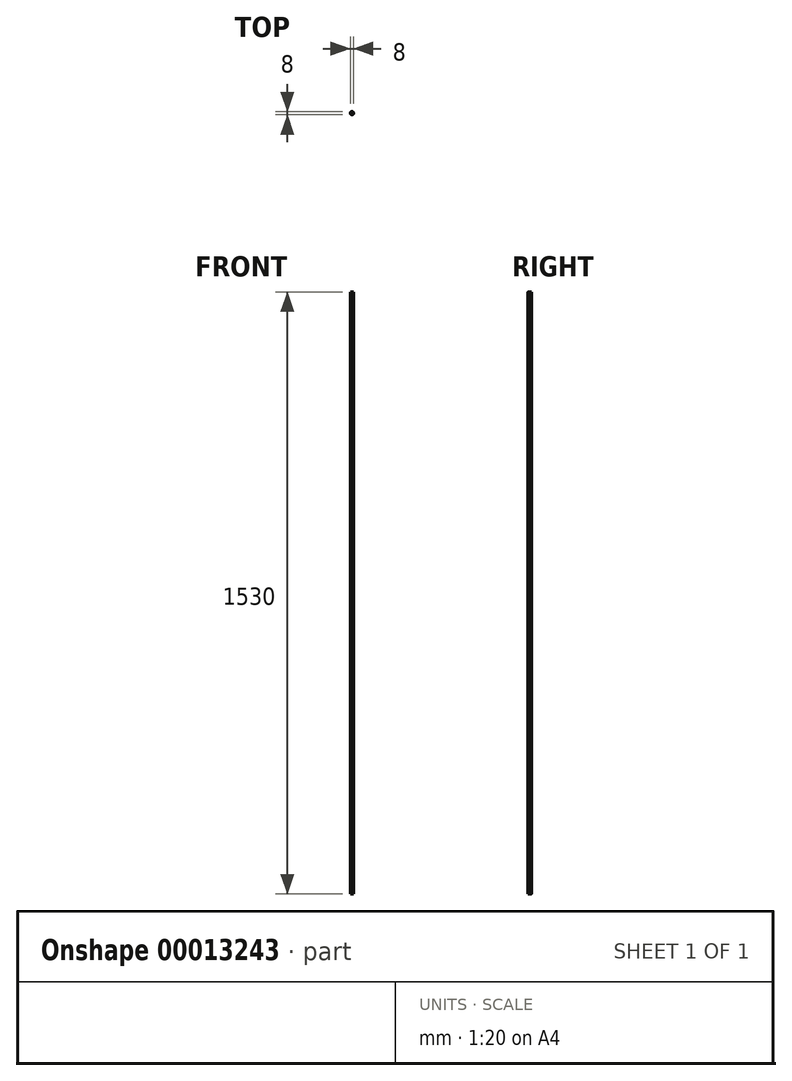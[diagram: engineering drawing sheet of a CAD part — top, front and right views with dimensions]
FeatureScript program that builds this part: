
annotation { "Feature Type Name" : "Feature", "Feature Type Description" : "" }
export const myFeature = defineFeature(function(context is Context, id is Id, definition is map)
    precondition{}
    {
        {
            var Q0;
            Q0=qCreatedBy(makeId("Top.planeOp"),FACE);
            var sketch = newSketch(context, id + "F1", { "sketchPlane" : qUnion([Q0])});
            skCircle(sketch, "E0", {"center": v(0, 0) * mm, "radius": 4 * mm});
            skSolve(sketch);
        }
        {
            var Q0;
            Q0=makeQuery(id+"F1.imprint","IMPRINT",FACE,{"disambiguationData":[TD([[makeQuery(id+"F1.imprint","IMPRINT",EDGE,{"derivedFrom":sQuery(id+"F1.wireOp",EDGE,"E0")}),1.0]])]});
            extrude(context, id + "F0", {"entities" : qUnion([Q0]), "depth" : (1530 / 2) * mm, "hasSecondDirection" : true, "secondDirectionOppositeDirection" : true, "secondDirectionDepth" : 765 * mm});
        }
    });
